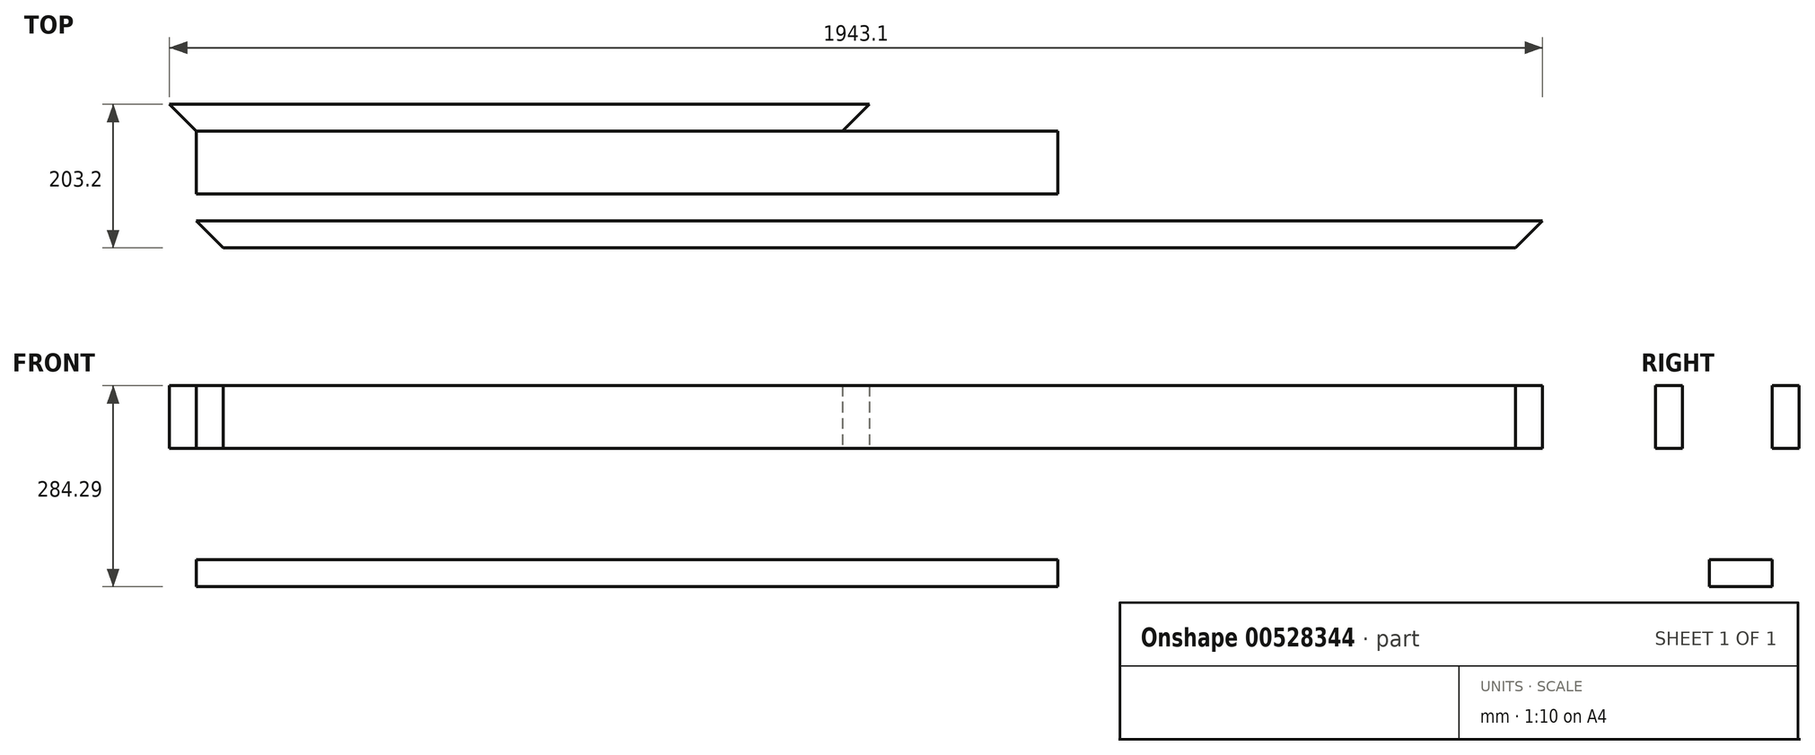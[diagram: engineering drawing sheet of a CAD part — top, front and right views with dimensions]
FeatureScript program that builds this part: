
annotation { "Feature Type Name" : "Feature", "Feature Type Description" : "" }
export const myFeature = defineFeature(function(context is Context, id is Id, definition is map)
    precondition{}
    {
        {
            var Q0;
            Q0=qCreatedBy(makeId("Top.planeOp"),FACE);
            var sketch = newSketch(context, id + "F0", { "sketchPlane" : qUnion([Q0])});
            skLineSegment(sketch, "E0", {"start": v(0, 0) * mm, "end": v(-38.1, 38.1) * mm});
            skLineSegment(sketch, "E1", {"start": v(-38.1, 38.1) * mm, "end": v(952.5, 38.1) * mm});
            skLineSegment(sketch, "E2", {"start": v(914.4, 0) * mm, "end": v(952.5, 38.1) * mm});
            skLineSegment(sketch, "E3", {"start": v(0, 0) * mm, "end": v(914.4, 0) * mm});
            skSolve(sketch);
        }
        {
            var Q0;
            Q0 = qSketchRegion(id + "F0", true);
            extrude(context, id + "F1", {"entities" : qUnion([Q0]), "depth" : 88.9 * mm, "offsetDistance" : 25.4 * mm});
        }
        {
            var Q0;
            Q0=qCreatedBy(makeId("Top.planeOp"),FACE);
            var sketch = newSketch(context, id + "F2", { "sketchPlane" : qUnion([Q0])});
            skLineSegment(sketch, "E4", {"start": v(38.1, -165.1) * mm, "end": v(1866.9, -165.1) * mm});
            skLineSegment(sketch, "E5", {"start": v(1866.9, -165.1) * mm, "end": v(1905, -127) * mm});
            skLineSegment(sketch, "E6", {"start": v(38.1, -165.1) * mm, "end": v(0, -127) * mm});
            skLineSegment(sketch, "E7", {"start": v(0, -127) * mm, "end": v(1905, -127) * mm});
            skSolve(sketch);
        }
        {
            var Q0;
            Q0 = qSketchRegion(id + "F2", true);
            extrude(context, id + "F3", {"entities" : qUnion([Q0]), "depth" : 88.9 * mm, "offsetDistance" : 25.4 * mm});
        }
        {
            var Q0;
            Q0=qCreatedBy(makeId("Front.planeOp"),FACE);
            var sketch = newSketch(context, id + "F4", { "sketchPlane" : qUnion([Q0])});
            skLineSegment(sketch, "E8", {"start": v(0, -157.29) * mm, "end": v(1219.2, -157.29) * mm});
            skLineSegment(sketch, "E9", {"start": v(0, -157.29) * mm, "end": v(0, -195.39) * mm});
            skLineSegment(sketch, "E10", {"start": v(0, -195.39) * mm, "end": v(1219.2, -195.39) * mm});
            skLineSegment(sketch, "E11", {"start": v(1219.2, -157.29) * mm, "end": v(1219.2, -195.39) * mm});
            skSolve(sketch);
        }
        {
            var Q0;
            Q0 = qSketchRegion(id + "F4", true);
            extrude(context, id + "F5", {"entities" : qUnion([Q0]), "depth" : 88.9 * mm, "offsetDistance" : 25.4 * mm});
        }
    });
